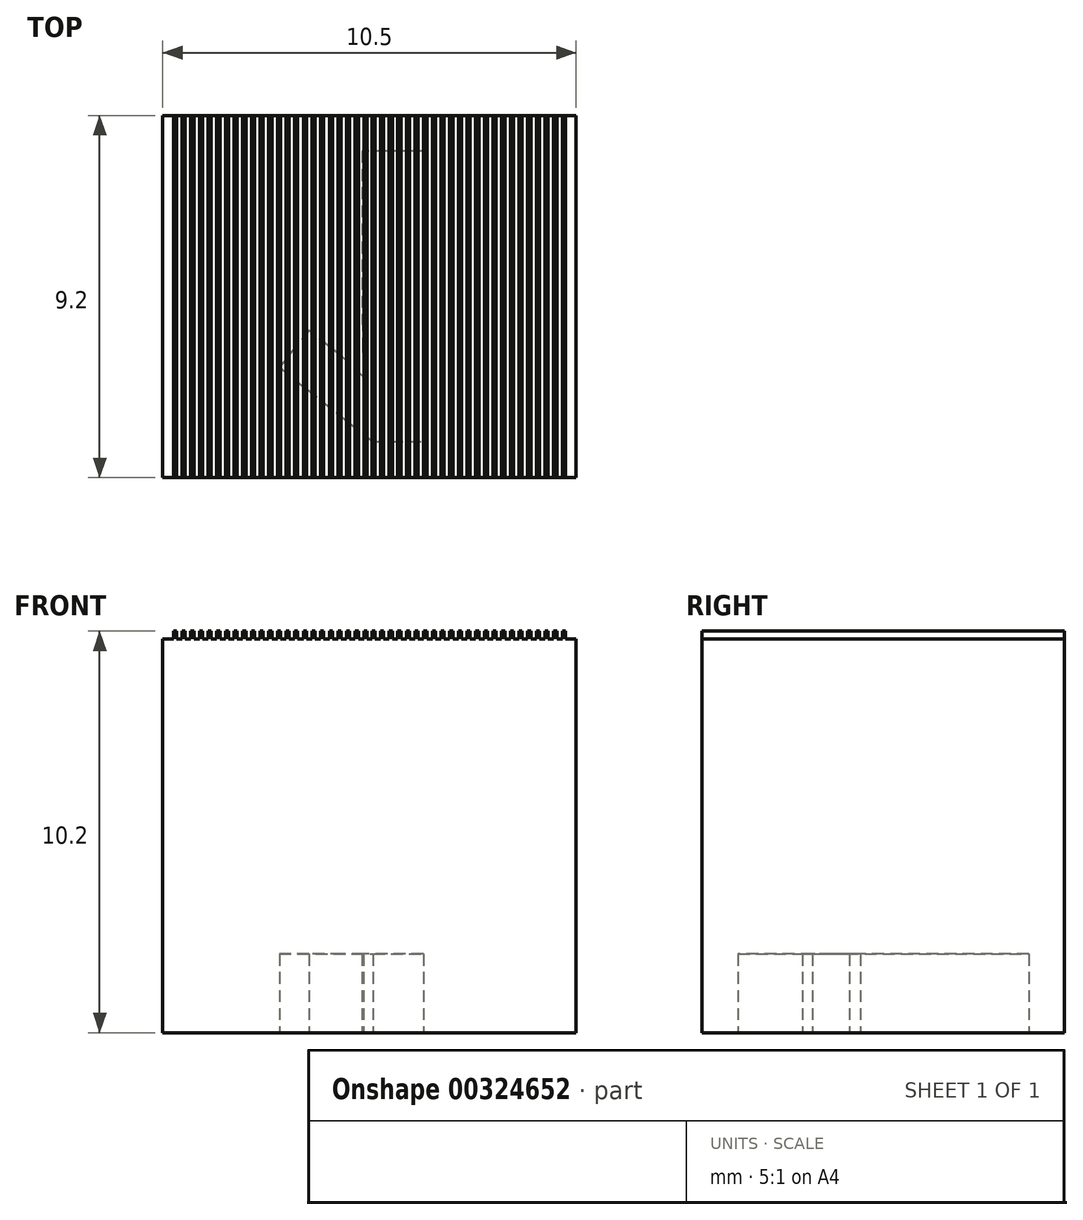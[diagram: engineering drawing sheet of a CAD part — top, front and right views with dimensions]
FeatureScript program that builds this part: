
annotation { "Feature Type Name" : "Feature", "Feature Type Description" : "" }
export const myFeature = defineFeature(function(context is Context, id is Id, definition is map)
    precondition{}
    {
        {
            assignVariable(context, id + "F0", {"name" : "h", "anyValue" : 10});
        }
        {
            assignVariable(context, id + "F1", {"name" : "gh", "anyValue" : 0.2});
        }
        {
            var Q0;
            Q0=qCreatedBy(makeId("Top.planeOp"),FACE);
            var sketch = newSketch(context, id + "F2", { "sketchPlane" : qUnion([Q0])});
            skLineSegment(sketch, "E0.bottom", {"start": v(5.25, 4.6) * mm, "end": v(-5.25, 4.6) * mm});
            skLineSegment(sketch, "E0.top", {"start": v(5.25, -4.6) * mm, "end": v(-5.25, -4.6) * mm});
            skLineSegment(sketch, "E0.left", {"start": v(5.25, 4.6) * mm, "end": v(5.25, -4.6) * mm});
            skLineSegment(sketch, "E0.right", {"start": v(-5.25, 4.6) * mm, "end": v(-5.25, -4.6) * mm});
            skPoint(sketch, "E0.middle", {"position": v(0, 0) * mm});
            skSolve(sketch);
        }
        {
            var Q0;
            Q0 = qSketchRegion(id + "F2", true);
            extrude(context, id + "F3", {"entities" : qUnion([Q0]), "depth" : (getVariable(context, 'h')) * mm});
        }
        {
            var Q0;
            Q0=makeQuery(id+"F3.opExtrude","CAP_FACE",FACE,{"disambiguationData":[OSD([sQuery(id+"F2.wireOp",EDGE,"E0.bottom"),sQuery(id+"F2.wireOp",EDGE,"E0.top"),sQuery(id+"F2.wireOp",EDGE,"E0.left"),sQuery(id+"F2.wireOp",EDGE,"E0.right")])],"isStart":false});
            var sketch = newSketch(context, id + "F4", { "sketchPlane" : qUnion([Q0])});
            skLineSegment(sketch, "E1", {"start": v(0.06, 4.6) * mm, "end": v(0.06, -4.6) * mm});
            skLineSegment(sketch, "E2", {"start": v(-0.06, -4.6) * mm, "end": v(-0.06, 4.6) * mm, "construction": true});
            skLineSegment(sketch, "E3", {"start": v(-3.01, 4.6) * mm, "end": v(-2.9, 4.6) * mm, "construction": true});
            skLineSegment(sketch, "E4", {"start": v(0.14, -4.6) * mm, "end": v(0.14, 4.6) * mm});
            skLineSegment(sketch, "E5", {"start": v(0.06, 0) * mm, "end": v(-0.06, 0) * mm, "construction": true});
            skPoint(sketch, "E6", {"position": v(0, 0) * mm});
            skLineSegment(sketch, "E7", {"start": v(0.06, 4.6) * mm, "end": v(0.14, 4.6) * mm});
            skLineSegment(sketch, "E8", {"start": v(0.14, -4.6) * mm, "end": v(0.06, -4.6) * mm});
            skLineSegment(sketch, "E9.1.0.0", {"start": v(0.28, 4.6) * mm, "end": v(0.36, 4.6) * mm});
            skLineSegment(sketch, "E9.1.0.1", {"start": v(0.36, -4.6) * mm, "end": v(0.36, 4.6) * mm});
            skLineSegment(sketch, "E9.1.0.2", {"start": v(0.28, 4.6) * mm, "end": v(0.28, -4.6) * mm});
            skLineSegment(sketch, "E9.1.0.3", {"start": v(0.36, -4.6) * mm, "end": v(0.28, -4.6) * mm});
            skLineSegment(sketch, "E9.2.0.0", {"start": v(0.5, 4.6) * mm, "end": v(0.58, 4.6) * mm});
            skLineSegment(sketch, "E9.2.0.1", {"start": v(0.58, -4.6) * mm, "end": v(0.58, 4.6) * mm});
            skLineSegment(sketch, "E9.2.0.2", {"start": v(0.5, 4.6) * mm, "end": v(0.5, -4.6) * mm});
            skLineSegment(sketch, "E9.2.0.3", {"start": v(0.58, -4.6) * mm, "end": v(0.5, -4.6) * mm});
            skLineSegment(sketch, "E9.3.0.0", {"start": v(0.72, 4.6) * mm, "end": v(0.8, 4.6) * mm});
            skLineSegment(sketch, "E9.3.0.1", {"start": v(0.8, -4.6) * mm, "end": v(0.8, 4.6) * mm});
            skLineSegment(sketch, "E9.3.0.2", {"start": v(0.72, 4.6) * mm, "end": v(0.72, -4.6) * mm});
            skLineSegment(sketch, "E9.3.0.3", {"start": v(0.8, -4.6) * mm, "end": v(0.72, -4.6) * mm});
            skLineSegment(sketch, "E9.4.0.0", {"start": v(0.94, 4.6) * mm, "end": v(1.02, 4.6) * mm});
            skLineSegment(sketch, "E9.4.0.1", {"start": v(1.02, -4.6) * mm, "end": v(1.02, 4.6) * mm});
            skLineSegment(sketch, "E9.4.0.2", {"start": v(0.94, 4.6) * mm, "end": v(0.94, -4.6) * mm});
            skLineSegment(sketch, "E9.4.0.3", {"start": v(1.02, -4.6) * mm, "end": v(0.94, -4.6) * mm});
            skLineSegment(sketch, "E9.5.0.0", {"start": v(1.16, 4.6) * mm, "end": v(1.24, 4.6) * mm});
            skLineSegment(sketch, "E9.5.0.1", {"start": v(1.24, -4.6) * mm, "end": v(1.24, 4.6) * mm});
            skLineSegment(sketch, "E9.5.0.2", {"start": v(1.16, 4.6) * mm, "end": v(1.16, -4.6) * mm});
            skLineSegment(sketch, "E9.5.0.3", {"start": v(1.24, -4.6) * mm, "end": v(1.16, -4.6) * mm});
            skLineSegment(sketch, "E9.6.0.0", {"start": v(1.38, 4.6) * mm, "end": v(1.46, 4.6) * mm});
            skLineSegment(sketch, "E9.6.0.1", {"start": v(1.46, -4.6) * mm, "end": v(1.46, 4.6) * mm});
            skLineSegment(sketch, "E9.6.0.2", {"start": v(1.38, 4.6) * mm, "end": v(1.38, -4.6) * mm});
            skLineSegment(sketch, "E9.6.0.3", {"start": v(1.46, -4.6) * mm, "end": v(1.38, -4.6) * mm});
            skLineSegment(sketch, "E9.7.0.0", {"start": v(1.6, 4.6) * mm, "end": v(1.68, 4.6) * mm});
            skLineSegment(sketch, "E9.7.0.1", {"start": v(1.68, -4.6) * mm, "end": v(1.68, 4.6) * mm});
            skLineSegment(sketch, "E9.7.0.2", {"start": v(1.6, 4.6) * mm, "end": v(1.6, -4.6) * mm});
            skLineSegment(sketch, "E9.7.0.3", {"start": v(1.68, -4.6) * mm, "end": v(1.6, -4.6) * mm});
            skLineSegment(sketch, "E9.8.0.0", {"start": v(1.82, 4.6) * mm, "end": v(1.9, 4.6) * mm});
            skLineSegment(sketch, "E9.8.0.1", {"start": v(1.9, -4.6) * mm, "end": v(1.9, 4.6) * mm});
            skLineSegment(sketch, "E9.8.0.2", {"start": v(1.82, 4.6) * mm, "end": v(1.82, -4.6) * mm});
            skLineSegment(sketch, "E9.8.0.3", {"start": v(1.9, -4.6) * mm, "end": v(1.82, -4.6) * mm});
            skLineSegment(sketch, "E9.9.0.0", {"start": v(2.04, 4.6) * mm, "end": v(2.12, 4.6) * mm});
            skLineSegment(sketch, "E9.9.0.1", {"start": v(2.12, -4.6) * mm, "end": v(2.12, 4.6) * mm});
            skLineSegment(sketch, "E9.9.0.2", {"start": v(2.04, 4.6) * mm, "end": v(2.04, -4.6) * mm});
            skLineSegment(sketch, "E9.9.0.3", {"start": v(2.12, -4.6) * mm, "end": v(2.04, -4.6) * mm});
            skLineSegment(sketch, "E9.direction1", {"start": v(0.06, 4.6) * mm, "end": v(0.28, 4.6) * mm, "construction": true});
            skLineSegment(sketch, "E10.0.10.0", {"start": v(2.26, 4.6) * mm, "end": v(2.34, 4.6) * mm});
            skLineSegment(sketch, "E10.3.10.0", {"start": v(2.34, -4.6) * mm, "end": v(2.34, 4.6) * mm});
            skLineSegment(sketch, "E10.6.10.0", {"start": v(2.26, 4.6) * mm, "end": v(2.26, -4.6) * mm});
            skLineSegment(sketch, "E10.9.10.0", {"start": v(2.34, -4.6) * mm, "end": v(2.26, -4.6) * mm});
            skLineSegment(sketch, "E11.0.11.0", {"start": v(2.48, 4.6) * mm, "end": v(2.56, 4.6) * mm});
            skLineSegment(sketch, "E11.3.11.0", {"start": v(2.56, -4.6) * mm, "end": v(2.56, 4.6) * mm});
            skLineSegment(sketch, "E11.6.11.0", {"start": v(2.48, 4.6) * mm, "end": v(2.48, -4.6) * mm});
            skLineSegment(sketch, "E11.9.11.0", {"start": v(2.56, -4.6) * mm, "end": v(2.48, -4.6) * mm});
            skLineSegment(sketch, "E12.0.12.0", {"start": v(2.7, 4.6) * mm, "end": v(2.78, 4.6) * mm});
            skLineSegment(sketch, "E12.3.12.0", {"start": v(2.78, -4.6) * mm, "end": v(2.78, 4.6) * mm});
            skLineSegment(sketch, "E12.6.12.0", {"start": v(2.7, 4.6) * mm, "end": v(2.7, -4.6) * mm});
            skLineSegment(sketch, "E12.9.12.0", {"start": v(2.78, -4.6) * mm, "end": v(2.7, -4.6) * mm});
            skLineSegment(sketch, "E13.0.13.0", {"start": v(2.92, 4.6) * mm, "end": v(3, 4.6) * mm});
            skLineSegment(sketch, "E13.3.13.0", {"start": v(3, -4.6) * mm, "end": v(3, 4.6) * mm});
            skLineSegment(sketch, "E13.6.13.0", {"start": v(2.92, 4.6) * mm, "end": v(2.92, -4.6) * mm});
            skLineSegment(sketch, "E13.9.13.0", {"start": v(3, -4.6) * mm, "end": v(2.92, -4.6) * mm});
            skLineSegment(sketch, "E14.0.14.0", {"start": v(3.14, 4.6) * mm, "end": v(3.22, 4.6) * mm});
            skLineSegment(sketch, "E14.3.14.0", {"start": v(3.22, -4.6) * mm, "end": v(3.22, 4.6) * mm});
            skLineSegment(sketch, "E14.6.14.0", {"start": v(3.14, 4.6) * mm, "end": v(3.14, -4.6) * mm});
            skLineSegment(sketch, "E14.9.14.0", {"start": v(3.22, -4.6) * mm, "end": v(3.14, -4.6) * mm});
            skLineSegment(sketch, "E15.0.15.0", {"start": v(3.36, 4.6) * mm, "end": v(3.44, 4.6) * mm});
            skLineSegment(sketch, "E15.3.15.0", {"start": v(3.44, -4.6) * mm, "end": v(3.44, 4.6) * mm});
            skLineSegment(sketch, "E15.6.15.0", {"start": v(3.36, 4.6) * mm, "end": v(3.36, -4.6) * mm});
            skLineSegment(sketch, "E15.9.15.0", {"start": v(3.44, -4.6) * mm, "end": v(3.36, -4.6) * mm});
            skLineSegment(sketch, "E15.0.16.0", {"start": v(3.58, 4.6) * mm, "end": v(3.66, 4.6) * mm});
            skLineSegment(sketch, "E15.3.16.0", {"start": v(3.66, -4.6) * mm, "end": v(3.66, 4.6) * mm});
            skLineSegment(sketch, "E15.6.16.0", {"start": v(3.58, 4.6) * mm, "end": v(3.58, -4.6) * mm});
            skLineSegment(sketch, "E15.9.16.0", {"start": v(3.66, -4.6) * mm, "end": v(3.58, -4.6) * mm});
            skLineSegment(sketch, "E16.0.17.0", {"start": v(3.8, 4.6) * mm, "end": v(3.88, 4.6) * mm});
            skLineSegment(sketch, "E16.3.17.0", {"start": v(3.88, -4.6) * mm, "end": v(3.88, 4.6) * mm});
            skLineSegment(sketch, "E16.6.17.0", {"start": v(3.8, 4.6) * mm, "end": v(3.8, -4.6) * mm});
            skLineSegment(sketch, "E16.9.17.0", {"start": v(3.88, -4.6) * mm, "end": v(3.8, -4.6) * mm});
            skLineSegment(sketch, "E16.0.18.0", {"start": v(4.02, 4.6) * mm, "end": v(4.1, 4.6) * mm});
            skLineSegment(sketch, "E16.3.18.0", {"start": v(4.1, -4.6) * mm, "end": v(4.1, 4.6) * mm});
            skLineSegment(sketch, "E16.6.18.0", {"start": v(4.02, 4.6) * mm, "end": v(4.02, -4.6) * mm});
            skLineSegment(sketch, "E16.9.18.0", {"start": v(4.1, -4.6) * mm, "end": v(4.02, -4.6) * mm});
            skLineSegment(sketch, "E17.0.19.0", {"start": v(4.24, 4.6) * mm, "end": v(4.32, 4.6) * mm});
            skLineSegment(sketch, "E17.3.19.0", {"start": v(4.32, -4.6) * mm, "end": v(4.32, 4.6) * mm});
            skLineSegment(sketch, "E17.6.19.0", {"start": v(4.24, 4.6) * mm, "end": v(4.24, -4.6) * mm});
            skLineSegment(sketch, "E17.9.19.0", {"start": v(4.32, -4.6) * mm, "end": v(4.24, -4.6) * mm});
            skLineSegment(sketch, "E17.0.20.0", {"start": v(4.46, 4.6) * mm, "end": v(4.54, 4.6) * mm});
            skLineSegment(sketch, "E17.3.20.0", {"start": v(4.54, -4.6) * mm, "end": v(4.54, 4.6) * mm});
            skLineSegment(sketch, "E17.6.20.0", {"start": v(4.46, 4.6) * mm, "end": v(4.46, -4.6) * mm});
            skLineSegment(sketch, "E17.9.20.0", {"start": v(4.54, -4.6) * mm, "end": v(4.46, -4.6) * mm});
            skLineSegment(sketch, "E18.0.21.0", {"start": v(4.68, 4.6) * mm, "end": v(4.76, 4.6) * mm});
            skLineSegment(sketch, "E18.3.21.0", {"start": v(4.76, -4.6) * mm, "end": v(4.76, 4.6) * mm});
            skLineSegment(sketch, "E18.6.21.0", {"start": v(4.68, 4.6) * mm, "end": v(4.68, -4.6) * mm});
            skLineSegment(sketch, "E18.9.21.0", {"start": v(4.76, -4.6) * mm, "end": v(4.68, -4.6) * mm});
            skLineSegment(sketch, "E19.0.22.0", {"start": v(4.9, 4.6) * mm, "end": v(4.98, 4.6) * mm});
            skLineSegment(sketch, "E19.3.22.0", {"start": v(4.98, -4.6) * mm, "end": v(4.98, 4.6) * mm});
            skLineSegment(sketch, "E19.6.22.0", {"start": v(4.9, 4.6) * mm, "end": v(4.9, -4.6) * mm});
            skLineSegment(sketch, "E19.9.22.0", {"start": v(4.98, -4.6) * mm, "end": v(4.9, -4.6) * mm});
            skLineSegment(sketch, "E20.MirrorCS", {"start": v(-0.28, 4.6) * mm, "end": v(-0.36, 4.6) * mm});
            skLineSegment(sketch, "E21.MirrorCS", {"start": v(-0.06, 4.6) * mm, "end": v(-0.14, 4.6) * mm});
            skLineSegment(sketch, "E22.MirrorCS", {"start": v(-3.8, 4.6) * mm, "end": v(-3.88, 4.6) * mm});
            skLineSegment(sketch, "E23.MirrorCS", {"start": v(-2.12, -4.6) * mm, "end": v(-2.04, -4.6) * mm});
            skLineSegment(sketch, "E24.MirrorCS", {"start": v(-2.92, 4.6) * mm, "end": v(-3, 4.6) * mm});
            skLineSegment(sketch, "E25.MirrorCS", {"start": v(-1.38, 4.6) * mm, "end": v(-1.46, 4.6) * mm});
            skLineSegment(sketch, "E26.MirrorCS", {"start": v(-1.68, -4.6) * mm, "end": v(-1.6, -4.6) * mm});
            skLineSegment(sketch, "E27.MirrorCS", {"start": v(-1.24, -4.6) * mm, "end": v(-1.16, -4.6) * mm});
            skLineSegment(sketch, "E28.MirrorCS", {"start": v(-4.1, -4.6) * mm, "end": v(-4.02, -4.6) * mm});
            skLineSegment(sketch, "E29.MirrorCS", {"start": v(-4.98, -4.6) * mm, "end": v(-4.9, -4.6) * mm});
            skLineSegment(sketch, "E30.MirrorCS", {"start": v(-2.7, 4.6) * mm, "end": v(-2.78, 4.6) * mm});
            skLineSegment(sketch, "E31.MirrorCS", {"start": v(-0.72, 4.6) * mm, "end": v(-0.8, 4.6) * mm});
            skLineSegment(sketch, "E32.MirrorCS", {"start": v(-1.6, 4.6) * mm, "end": v(-1.68, 4.6) * mm});
            skLineSegment(sketch, "E33.MirrorCS", {"start": v(-4.68, 4.6) * mm, "end": v(-4.76, 4.6) * mm});
            skLineSegment(sketch, "E34.MirrorCS", {"start": v(-3.58, 4.6) * mm, "end": v(-3.66, 4.6) * mm});
            skLineSegment(sketch, "E35.MirrorCS", {"start": v(-0.14, -4.6) * mm, "end": v(-0.06, -4.6) * mm});
            skLineSegment(sketch, "E36.MirrorCS", {"start": v(-4.02, 4.6) * mm, "end": v(-4.1, 4.6) * mm});
            skLineSegment(sketch, "E37.MirrorCS", {"start": v(-2.26, 4.6) * mm, "end": v(-2.34, 4.6) * mm});
            skLineSegment(sketch, "E38.MirrorCS", {"start": v(-3.14, 4.6) * mm, "end": v(-3.22, 4.6) * mm});
            skLineSegment(sketch, "E39.MirrorCS", {"start": v(-2.56, -4.6) * mm, "end": v(-2.48, -4.6) * mm});
            skLineSegment(sketch, "E40.MirrorCS", {"start": v(-4.32, -4.6) * mm, "end": v(-4.24, -4.6) * mm});
            skLineSegment(sketch, "E41.MirrorCS", {"start": v(-4.9, 4.6) * mm, "end": v(-4.98, 4.6) * mm});
            skLineSegment(sketch, "E42.MirrorCS", {"start": v(-3.44, -4.6) * mm, "end": v(-3.36, -4.6) * mm});
            skLineSegment(sketch, "E43.MirrorCS", {"start": v(-0.94, 4.6) * mm, "end": v(-1.02, 4.6) * mm});
            skLineSegment(sketch, "E44.MirrorCS", {"start": v(-3.66, -4.6) * mm, "end": v(-3.58, -4.6) * mm});
            skLineSegment(sketch, "E45.MirrorCS", {"start": v(-2.78, -4.6) * mm, "end": v(-2.7, -4.6) * mm});
            skLineSegment(sketch, "E46.MirrorCS", {"start": v(-1.16, 4.6) * mm, "end": v(-1.24, 4.6) * mm});
            skLineSegment(sketch, "E47.MirrorCS", {"start": v(-4.54, -4.6) * mm, "end": v(-4.46, -4.6) * mm});
            skLineSegment(sketch, "E48.MirrorCS", {"start": v(-2.04, 4.6) * mm, "end": v(-2.12, 4.6) * mm});
            skLineSegment(sketch, "E49.MirrorCS", {"start": v(-1.02, -4.6) * mm, "end": v(-0.94, -4.6) * mm});
            skLineSegment(sketch, "E50.MirrorCS", {"start": v(-1.82, 4.6) * mm, "end": v(-1.9, 4.6) * mm});
            skLineSegment(sketch, "E51.MirrorCS", {"start": v(-0.8, -4.6) * mm, "end": v(-0.72, -4.6) * mm});
            skLineSegment(sketch, "E52.MirrorCS", {"start": v(-4.46, 4.6) * mm, "end": v(-4.54, 4.6) * mm});
            skLineSegment(sketch, "E53.MirrorCS", {"start": v(-1.46, -4.6) * mm, "end": v(-1.38, -4.6) * mm});
            skLineSegment(sketch, "E54.MirrorCS", {"start": v(-0.58, -4.6) * mm, "end": v(-0.5, -4.6) * mm});
            skLineSegment(sketch, "E55.MirrorCS", {"start": v(-4.76, -4.6) * mm, "end": v(-4.68, -4.6) * mm});
            skLineSegment(sketch, "E56.MirrorCS", {"start": v(-3.88, -4.6) * mm, "end": v(-3.8, -4.6) * mm});
            skLineSegment(sketch, "E57.MirrorCS", {"start": v(-3, -4.6) * mm, "end": v(-2.92, -4.6) * mm});
            skLineSegment(sketch, "E58.MirrorCS", {"start": v(-0.06, 4.6) * mm, "end": v(-0.28, 4.6) * mm, "construction": true});
            skLineSegment(sketch, "E59.MirrorCS", {"start": v(-0.36, -4.6) * mm, "end": v(-0.28, -4.6) * mm});
            skLineSegment(sketch, "E60.MirrorCS", {"start": v(-0.5, 4.6) * mm, "end": v(-0.58, 4.6) * mm});
            skLineSegment(sketch, "E61.MirrorCS", {"start": v(-3.22, -4.6) * mm, "end": v(-3.14, -4.6) * mm});
            skLineSegment(sketch, "E62.MirrorCS", {"start": v(-2.34, -4.6) * mm, "end": v(-2.26, -4.6) * mm});
            skLineSegment(sketch, "E63.MirrorCS", {"start": v(-1.9, -4.6) * mm, "end": v(-1.82, -4.6) * mm});
            skLineSegment(sketch, "E64.MirrorCS", {"start": v(-3.36, 4.6) * mm, "end": v(-3.44, 4.6) * mm});
            skLineSegment(sketch, "E65.MirrorCS", {"start": v(-4.24, 4.6) * mm, "end": v(-4.32, 4.6) * mm});
            skLineSegment(sketch, "E66.MirrorCS", {"start": v(-0.06, 0) * mm, "end": v(0.06, 0) * mm, "construction": true});
            skLineSegment(sketch, "E67.MirrorCS", {"start": v(-2.48, 4.6) * mm, "end": v(-2.56, 4.6) * mm});
            skLineSegment(sketch, "E68.MirrorCS", {"start": v(-4.68, 4.6) * mm, "end": v(-4.68, -4.6) * mm});
            skLineSegment(sketch, "E69.MirrorCS", {"start": v(-3.8, 4.6) * mm, "end": v(-3.8, -4.6) * mm});
            skLineSegment(sketch, "E70.MirrorCS", {"start": v(-4.32, -4.6) * mm, "end": v(-4.32, 4.6) * mm});
            skLineSegment(sketch, "E71.MirrorCS", {"start": v(-2.92, 4.6) * mm, "end": v(-2.92, -4.6) * mm});
            skLineSegment(sketch, "E72.MirrorCS", {"start": v(-3.44, -4.6) * mm, "end": v(-3.44, 4.6) * mm});
            skLineSegment(sketch, "E73.MirrorCS", {"start": v(-2.56, -4.6) * mm, "end": v(-2.56, 4.6) * mm});
            skLineSegment(sketch, "E74.MirrorCS", {"start": v(-2.12, -4.6) * mm, "end": v(-2.12, 4.6) * mm});
            skLineSegment(sketch, "E75.MirrorCS", {"start": v(-3.88, -4.6) * mm, "end": v(-3.88, 4.6) * mm});
            skLineSegment(sketch, "E76.MirrorCS", {"start": v(-3, -4.6) * mm, "end": v(-3, 4.6) * mm});
            skLineSegment(sketch, "E77.MirrorCS", {"start": v(-2.04, 4.6) * mm, "end": v(-2.04, -4.6) * mm});
            skLineSegment(sketch, "E78.MirrorCS", {"start": v(-1.16, 4.6) * mm, "end": v(-1.16, -4.6) * mm});
            skLineSegment(sketch, "E79.MirrorCS", {"start": v(-4.76, -4.6) * mm, "end": v(-4.76, 4.6) * mm});
            skLineSegment(sketch, "E80.MirrorCS", {"start": v(-1.38, 4.6) * mm, "end": v(-1.38, -4.6) * mm});
            skLineSegment(sketch, "E81.MirrorCS", {"start": v(-0.5, 4.6) * mm, "end": v(-0.5, -4.6) * mm});
            skLineSegment(sketch, "E82.MirrorCS", {"start": v(-1.02, -4.6) * mm, "end": v(-1.02, 4.6) * mm});
            skLineSegment(sketch, "E83.MirrorCS", {"start": v(-1.9, -4.6) * mm, "end": v(-1.9, 4.6) * mm});
            skLineSegment(sketch, "E84.MirrorCS", {"start": v(-1.6, 4.6) * mm, "end": v(-1.6, -4.6) * mm});
            skLineSegment(sketch, "E85.MirrorCS", {"start": v(-2.34, -4.6) * mm, "end": v(-2.34, 4.6) * mm});
            skLineSegment(sketch, "E86.MirrorCS", {"start": v(-0.06, 4.6) * mm, "end": v(-0.06, -4.6) * mm});
            skLineSegment(sketch, "E87.MirrorCS", {"start": v(-3.22, -4.6) * mm, "end": v(-3.22, 4.6) * mm});
            skLineSegment(sketch, "E88.MirrorCS", {"start": v(-4.98, -4.6) * mm, "end": v(-4.98, 4.6) * mm});
            skLineSegment(sketch, "E89.MirrorCS", {"start": v(-0.14, -4.6) * mm, "end": v(-0.14, 4.6) * mm});
            skLineSegment(sketch, "E90.MirrorCS", {"start": v(-4.46, 4.6) * mm, "end": v(-4.46, -4.6) * mm});
            skLineSegment(sketch, "E91.MirrorCS", {"start": v(-0.28, 4.6) * mm, "end": v(-0.28, -4.6) * mm});
            skLineSegment(sketch, "E92.MirrorCS", {"start": v(-1.46, -4.6) * mm, "end": v(-1.46, 4.6) * mm});
            skLineSegment(sketch, "E93.MirrorCS", {"start": v(-1.68, -4.6) * mm, "end": v(-1.68, 4.6) * mm});
            skLineSegment(sketch, "E94.MirrorCS", {"start": v(-0.8, -4.6) * mm, "end": v(-0.8, 4.6) * mm});
            skLineSegment(sketch, "E95.MirrorCS", {"start": v(-3.58, 4.6) * mm, "end": v(-3.58, -4.6) * mm});
            skLineSegment(sketch, "E96.MirrorCS", {"start": v(-0.36, -4.6) * mm, "end": v(-0.36, 4.6) * mm});
            skLineSegment(sketch, "E97.MirrorCS", {"start": v(-2.7, 4.6) * mm, "end": v(-2.7, -4.6) * mm});
            skLineSegment(sketch, "E98.MirrorCS", {"start": v(-3.66, -4.6) * mm, "end": v(-3.66, 4.6) * mm});
            skLineSegment(sketch, "E99.MirrorCS", {"start": v(-2.78, -4.6) * mm, "end": v(-2.78, 4.6) * mm});
            skLineSegment(sketch, "E100.MirrorCS", {"start": v(-1.82, 4.6) * mm, "end": v(-1.82, -4.6) * mm});
            skLineSegment(sketch, "E101.MirrorCS", {"start": v(0.06, -4.6) * mm, "end": v(0.06, 4.6) * mm, "construction": true});
            skLineSegment(sketch, "E102.MirrorCS", {"start": v(-4.54, -4.6) * mm, "end": v(-4.54, 4.6) * mm});
            skLineSegment(sketch, "E103.MirrorCS", {"start": v(-0.94, 4.6) * mm, "end": v(-0.94, -4.6) * mm});
            skLineSegment(sketch, "E104.MirrorCS", {"start": v(-4.24, 4.6) * mm, "end": v(-4.24, -4.6) * mm});
            skLineSegment(sketch, "E105.MirrorCS", {"start": v(-3.36, 4.6) * mm, "end": v(-3.36, -4.6) * mm});
            skLineSegment(sketch, "E106.MirrorCS", {"start": v(-2.48, 4.6) * mm, "end": v(-2.48, -4.6) * mm});
            skLineSegment(sketch, "E107.MirrorCS", {"start": v(-4.9, 4.6) * mm, "end": v(-4.9, -4.6) * mm});
            skLineSegment(sketch, "E108.MirrorCS", {"start": v(-4.02, 4.6) * mm, "end": v(-4.02, -4.6) * mm});
            skLineSegment(sketch, "E109.MirrorCS", {"start": v(-3.14, 4.6) * mm, "end": v(-3.14, -4.6) * mm});
            skLineSegment(sketch, "E110.MirrorCS", {"start": v(-2.26, 4.6) * mm, "end": v(-2.26, -4.6) * mm});
            skLineSegment(sketch, "E111.MirrorCS", {"start": v(-0.72, 4.6) * mm, "end": v(-0.72, -4.6) * mm});
            skLineSegment(sketch, "E112.MirrorCS", {"start": v(-0.58, -4.6) * mm, "end": v(-0.58, 4.6) * mm});
            skLineSegment(sketch, "E113.MirrorCS", {"start": v(-4.1, -4.6) * mm, "end": v(-4.1, 4.6) * mm});
            skLineSegment(sketch, "E114.MirrorCS", {"start": v(-1.24, -4.6) * mm, "end": v(-1.24, 4.6) * mm});
            skSolve(sketch);
        }
        {
            var Q0;
            Q0 = qSketchRegion(id + "F4", true);
            extrude(context, id + "F5", {"entities" : qUnion([Q0]), "operationType" : NewBodyOperationType.ADD, "depth" : (getVariable(context, 'gh')) * mm});
        }
        {
            var Q0;
            Q0=makeQuery(id+"F3.opExtrude","CAP_FACE",FACE,{"disambiguationData":[OSD([sQuery(id+"F2.wireOp",EDGE,"E0.bottom"),sQuery(id+"F2.wireOp",EDGE,"E0.top"),sQuery(id+"F2.wireOp",EDGE,"E0.left"),sQuery(id+"F2.wireOp",EDGE,"E0.right")])],"isStart":true});
            var sketch = newSketch(context, id + "F6", { "sketchPlane" : qUnion([Q0])});
            skText(sketch, "E115", { "text": "1", "fontName": "OpenSans-Bold.ttf"});
            const initialGuessF6  = {"E115": [-0.0029, -0.0037, 1, 0, 0.00745]};
            skSetInitialGuess(sketch, initialGuessF6);
            skSolve(sketch);
        }
        {
            var Q0;
            Q0 = qSketchRegion(id + "F6", true);
            extrude(context, id + "F7", {"entities" : qUnion([Q0]), "operationType" : NewBodyOperationType.REMOVE, "oppositeDirection" : true, "depth" : 2 * mm});
        }
    });
